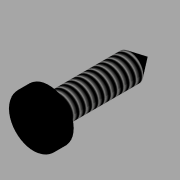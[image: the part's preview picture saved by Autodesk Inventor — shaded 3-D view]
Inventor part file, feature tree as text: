
AUTODESK INVENTOR PART (.ipt)
format: ipt  version: 2019 (Build 230136000, 136)  size: 135,680 bytes
history: native  units: mm
features: extrude x3, sketch x3, fillet x2, chamfer x1, thread x1
ambient origin geometry x8: Origin, YZ Plane, XZ Plane, XY Plane, X Axis, Y Axis, Z Axis, Center Point
bodies: Solid1 (feature_tree)
feature tree (10):
  extrude  "Extrusion1"  Depth=5.5mm TaperAngle=0.0deg
  extrude  "Extrusion2"  Depth=0.95mm TaperAngle=0.0deg
  chamfer  "Chamfer1"  Distance=0.75mm Angle=45.0deg
  fillet  "Fillet1"  Radius=0.2mm
  fillet  "Fillet2"  Radius=0.1mm
  extrude  "Extrusion3"  Depth=0.25mm
  thread  "Thread1"  [1 undecoded]
  sketch  "Sketch1"  dims[d0=1.5mm d1=5.5mm d2=0.0mm]
  sketch  "Sketch2"  dims[d3=2.85mm d4=0.95mm d5=0.0mm d6=0.75mm d7=1.0mm d8=45.0deg d9=0.2mm d10=0.1mm]
  sketch  "Sketch3"  dims[d11=2.5mm d12=0.25mm d13=0.25mm d14=2.5mm d15=0.25mm d16=0.0mm d17=10.0mm d18=0.0mm]
note: 1 required parameter value undecoded (feature->parameter linkage not recoverable at this tier; creation-order binding heuristic only, values carry confidence <= 0.55)
